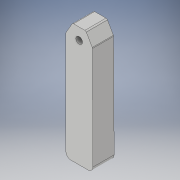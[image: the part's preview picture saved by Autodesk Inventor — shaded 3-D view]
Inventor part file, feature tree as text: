
AUTODESK INVENTOR PART (.ipt)
format: ipt  version: 2019 (Build 230136000, 136)  size: 114,688 bytes
history: native  units: mm
features: fillet x2, extrude x1, sketch x1
ambient origin geometry x8: Origin, YZ Plane, XZ Plane, XY Plane, X Axis, Y Axis, Z Axis, Center Point
bodies: Solid1 (feature_tree)
feature tree (4):
  extrude  "Extrusion1"  Depth=3.0mm
  fillet  "Fillet1"  Radius=16.3mm
  fillet  "Fillet2"  Radius=12.75mm
  sketch  "Sketch1"  dims[d0=4.0mm d2=65.0mm d3=16.3mm d4=12.75mm d5=0.0mm d6=1.0mm d7=3.0mm]
